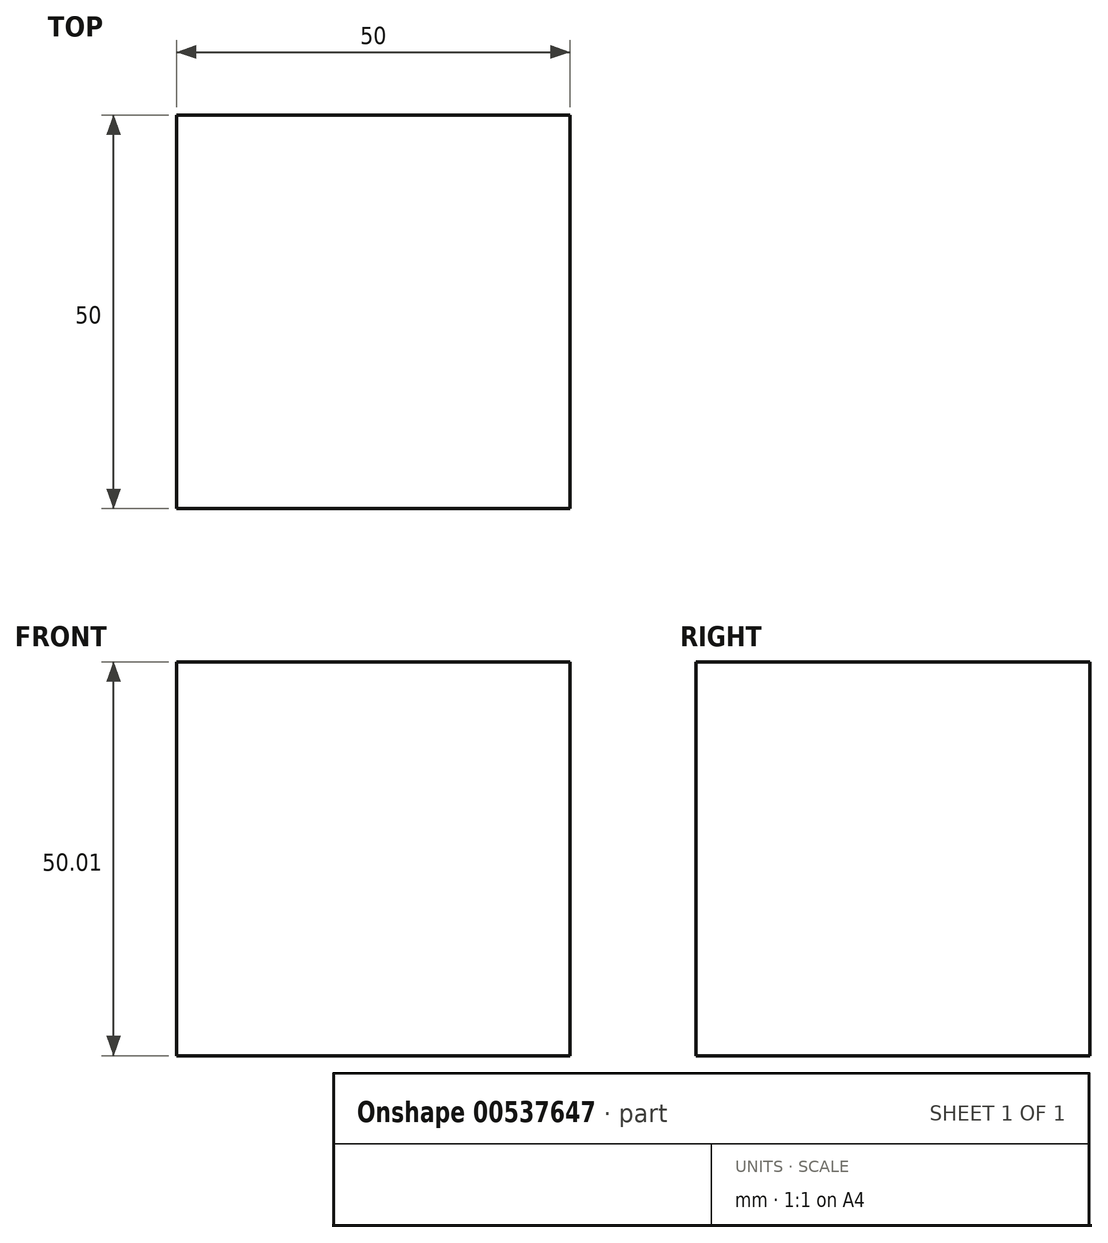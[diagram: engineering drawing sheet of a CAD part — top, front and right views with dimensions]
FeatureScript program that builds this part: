
annotation { "Feature Type Name" : "Feature", "Feature Type Description" : "" }
export const myFeature = defineFeature(function(context is Context, id is Id, definition is map)
    precondition{}
    {
        {
            var Q0;
            Q0=qCreatedBy(makeId("Top.planeOp"),FACE);
            var sketch = newSketch(context, id + "F0", { "sketchPlane" : qUnion([Q0])});
            skLineSegment(sketch, "E0.bottom", {"start": v(25, -25) * mm, "end": v(-25, -25) * mm});
            skLineSegment(sketch, "E0.top", {"start": v(25, 25) * mm, "end": v(-25, 25) * mm});
            skLineSegment(sketch, "E0.left", {"start": v(25, -25) * mm, "end": v(25, 25) * mm});
            skLineSegment(sketch, "E0.right", {"start": v(-25, -25) * mm, "end": v(-25, 25) * mm});
            skPoint(sketch, "E0.middle", {"position": v(0, 0) * mm});
            skSolve(sketch);
        }
        {
            var Q0;
            Q0 = qSketchRegion(id + "F0", true);
            extrude(context, id + "F1", {"entities" : qUnion([Q0]), "depth" : 50 * mm, "offsetDistance" : 25.4 * mm});
        }
    });
